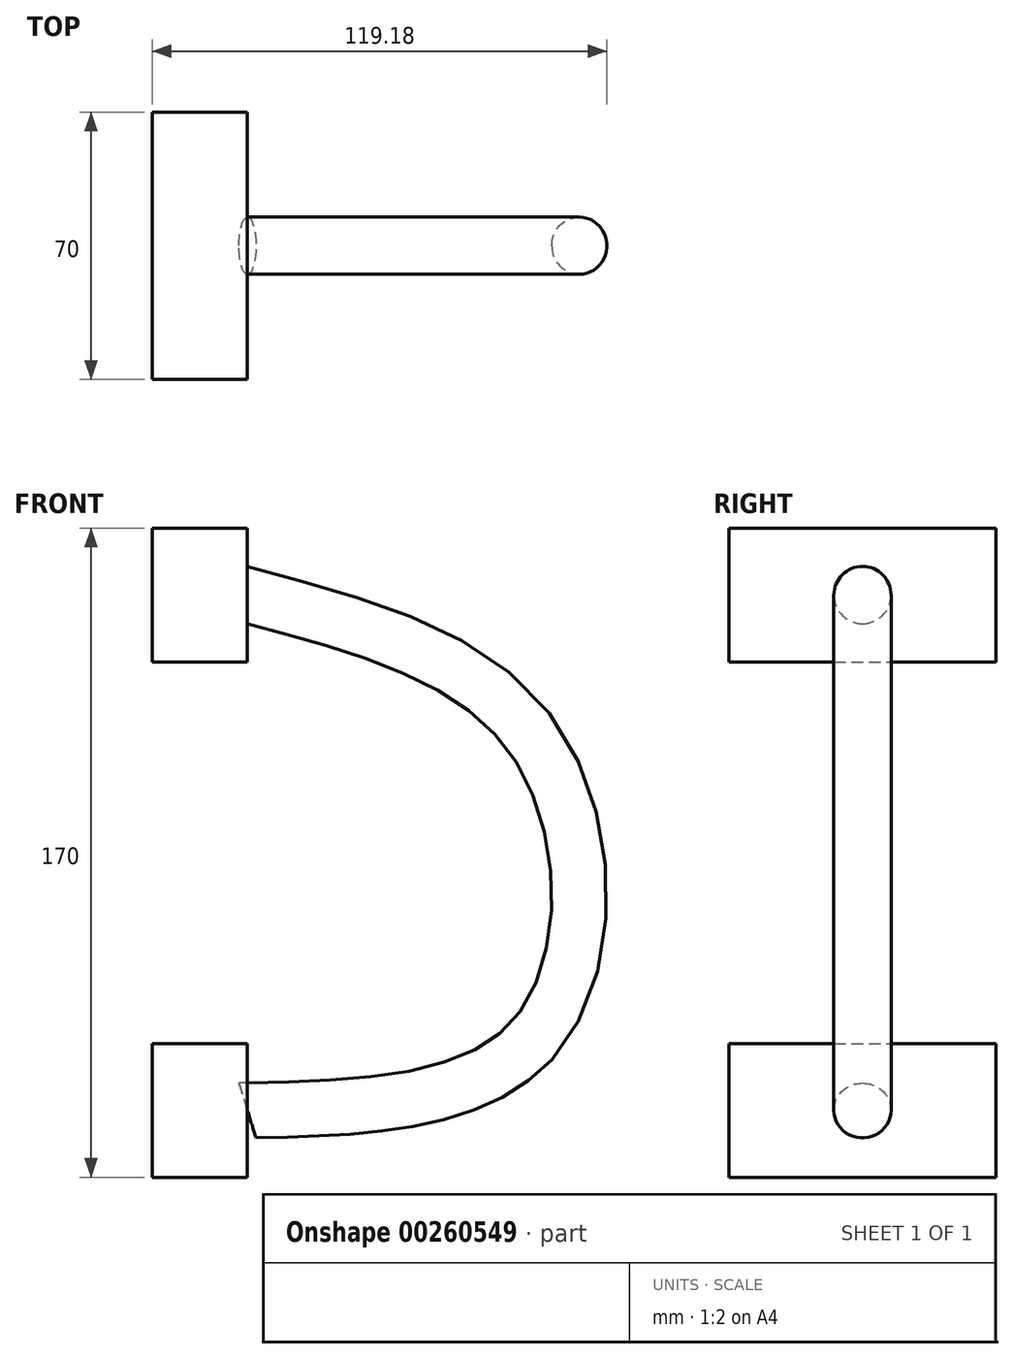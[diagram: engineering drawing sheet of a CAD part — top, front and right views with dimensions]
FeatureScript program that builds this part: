
annotation { "Feature Type Name" : "Feature", "Feature Type Description" : "" }
export const myFeature = defineFeature(function(context is Context, id is Id, definition is map)
    precondition{}
    {
        {
            var Q0;
            Q0=qCreatedBy(makeId("Front.planeOp"),FACE);
            var sketch = newSketch(context, id + "F0", { "sketchPlane" : qUnion([Q0])});
            skLineSegment(sketch, "E0.bottom", {"start": v(-35, 50) * mm, "end": v(-60, 50) * mm});
            skLineSegment(sketch, "E0.top", {"start": v(-35, 85) * mm, "end": v(-60, 85) * mm});
            skLineSegment(sketch, "E0.left", {"start": v(-35, 50) * mm, "end": v(-35, 85) * mm});
            skLineSegment(sketch, "E0.right", {"start": v(-60, 50) * mm, "end": v(-60, 85) * mm});
            skLineSegment(sketch, "E1.MirrorCS", {"start": v(-35, -50) * mm, "end": v(-60, -50) * mm});
            skLineSegment(sketch, "E2.MirrorCS", {"start": v(-35, -85) * mm, "end": v(-60, -85) * mm});
            skLineSegment(sketch, "E3.MirrorCS", {"start": v(-60, -50) * mm, "end": v(-60, -85) * mm});
            skLineSegment(sketch, "E4.MirrorCS", {"start": v(-35, -50) * mm, "end": v(-35, -85) * mm});
            skSolve(sketch);
        }
        {
            var Q0;
            Q0=makeQuery(id+"F0.imprint","IMPRINT",FACE,{"disambiguationData":[TD([[makeQuery(id+"F0.imprint","IMPRINT",EDGE,{"derivedFrom":sQuery(id+"F0.wireOp",EDGE,"E0.bottom")}),-1.0]])]});
            var Q1;
            Q1=makeQuery(id+"F0.imprint","IMPRINT",FACE,{"disambiguationData":[TD([[makeQuery(id+"F0.imprint","IMPRINT",EDGE,{"derivedFrom":sQuery(id+"F0.wireOp",EDGE,"E1.MirrorCS")}),1.0]])]});
            extrude(context, id + "F1", {"entities" : qUnion([Q0, Q1]), "depth" : 70 * mm, "symmetric" : true});
        }
        {
            var Q0;
            Q0=qCreatedBy(makeId("Front.planeOp"),FACE);
            var sketch = newSketch(context, id + "F2", { "sketchPlane" : qUnion([Q0])});
            skFitSpline(sketch, "E5", {"points": [v(-35, 67.5) * mm, v(39.72, 30.31) * mm, v(40.31, -48.23) * mm, v(-35, -67.5) * mm], "startDerivative": vector(230.87, -65.41) * mm, "endDerivative": vector(-245.6, -5.88) * mm});
            skSolve(sketch);
        }
        {
            var Q0;
            Q0=makeQuery(id+"F1.opExtrude","SWEPT_FACE",FACE,{"disambiguationData":[OSD([sQuery(id+"F0.wireOp",EDGE,"E0.left")])]});
            var sketch = newSketch(context, id + "F3", { "sketchPlane" : qUnion([Q0])});
            skPoint(sketch, "E6.0", {"position": v(0, 67.5) * mm});
            skPoint(sketch, "E7.0", {"position": v(0, -67.5) * mm});
            skCircle(sketch, "E8", {"center": v(0, 67.5) * mm, "radius": 7.5 * mm});
            skSolve(sketch);
        }
        {
            var Q0;
            Q0=makeQuery(id+"F3.imprint","IMPRINT",FACE,{"disambiguationData":[TD([[makeQuery(id+"F3.imprint","IMPRINT",EDGE,{"derivedFrom":sQuery(id+"F3.wireOp",EDGE,"E8")}),1.0]])]});
            var Q1;
            Q1=sQuery(id+"F2.wireOp",EDGE,"E5");
            sweep(context, id + "F4", {"profiles" : qUnion([Q0]), "path" : qUnion([Q1])});
        }
    });
